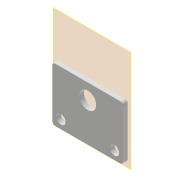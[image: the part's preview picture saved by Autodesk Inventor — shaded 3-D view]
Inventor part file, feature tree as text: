
AUTODESK INVENTOR PART (.ipt)
format: ipt  version: 2022 (Build 260153000, 153)  size: 105,984 bytes
history: native  units: mm
features: other x2, plane x1, extrude x1, sketch x1, reference x1
ambient origin geometry x8: Origin, YZ Plane, XZ Plane, XY Plane, X Axis, Y Axis, Z Axis, Center Point
bodies: Volumenkörper1 (feature_tree)
feature tree (6):
  plane  "Arbeitsebene1"
  extrude  "Extrusion1"  Depth=6.0mm
  sketch  "Skizze1"  dims[d0=6.0mm d1=6.0mm d2=11.0mm d3=25.0mm d4=35.0mm d5=0.0mm d6=2.0mm d7=3.0mm d8=0.0mm]
  reference  "Referenz1"
  other  "Anglerfish_lunchbox_m12large_flipped_v0.iam"
  other  "Anglerfish_coverslipclamp_top:1"
